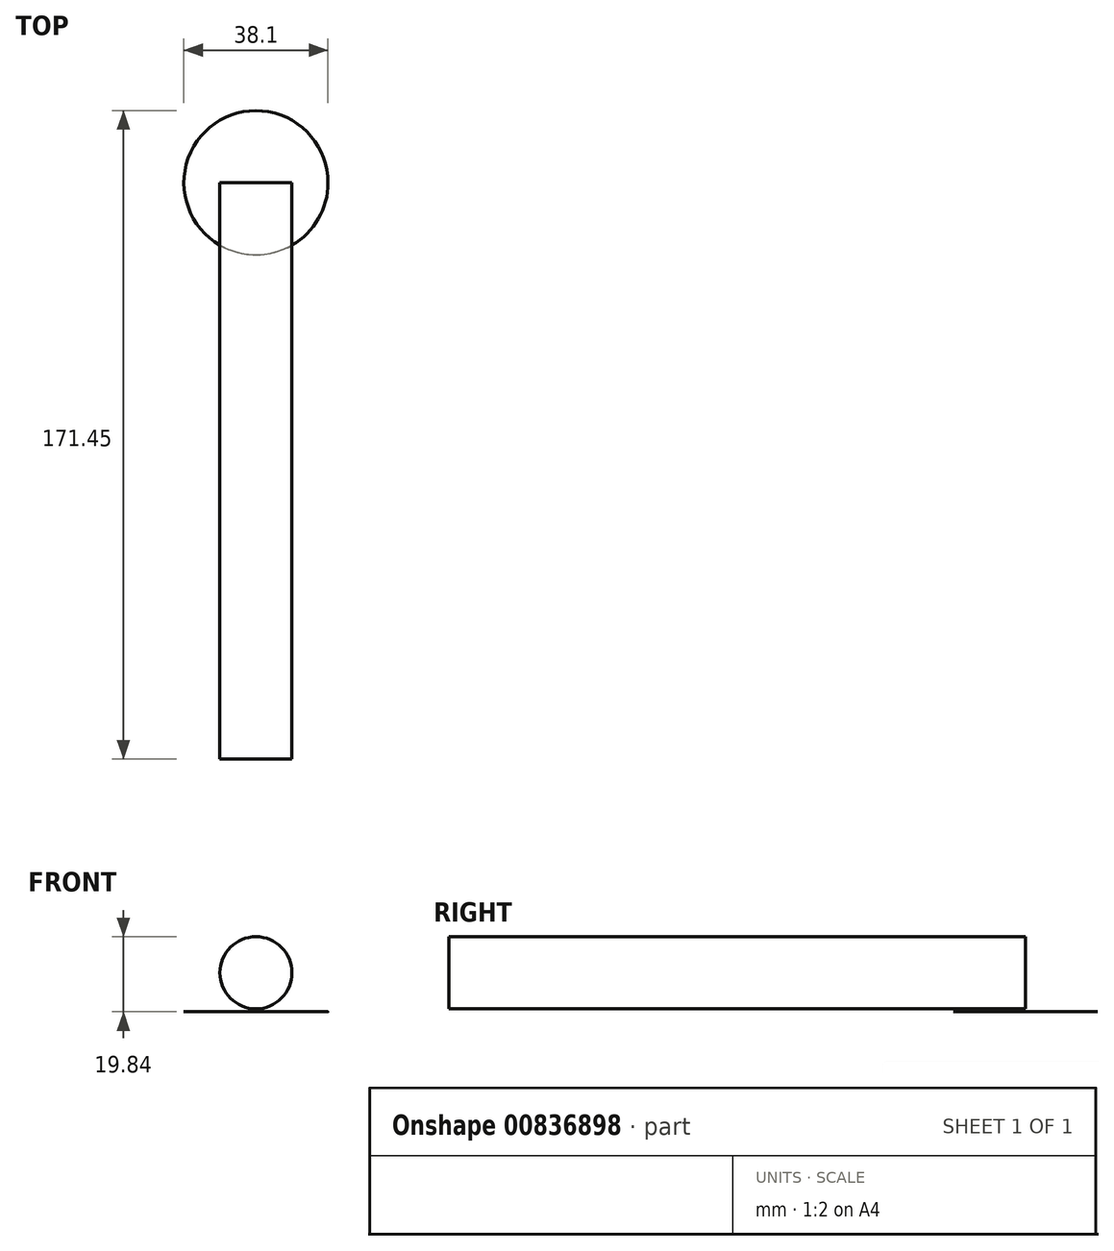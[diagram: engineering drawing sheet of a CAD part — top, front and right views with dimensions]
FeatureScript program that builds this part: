
annotation { "Feature Type Name" : "Feature", "Feature Type Description" : "" }
export const myFeature = defineFeature(function(context is Context, id is Id, definition is map)
    precondition{}
    {
        {
            var Q0;
            Q0=qCreatedBy(makeId("Top.planeOp"),FACE);
            var sketch = newSketch(context, id + "F0", { "sketchPlane" : qUnion([Q0])});
            skCircle(sketch, "E0", {"center": v(0, 0) * mm, "radius": 19.05 * mm});
            skSolve(sketch);
        }
        {
            var Q0;
            Q0=makeQuery(id+"F0.imprint","IMPRINT",FACE,{"disambiguationData":[TD([[makeQuery(id+"F0.imprint","IMPRINT",EDGE,{"derivedFrom":sQuery(id+"F0.wireOp",EDGE,"E0")}),1.0]])]});
            extrude(context, id + "F1", {"entities" : qUnion([Q0]), "depth" : 13 / 406.4 * mm, "offsetDistance" : 25.4 * mm});
        }
        {
            var Q0;
            Q0=qCreatedBy(makeId("Front.planeOp"),FACE);
            var sketch = newSketch(context, id + "F2", { "sketchPlane" : qUnion([Q0])});
            skCircle(sketch, "E1", {"center": v(0, 10.32) * mm, "radius": 9.53 * mm});
            skSolve(sketch);
        }
        {
            var Q0;
            Q0 = qSketchRegion(id + "F2", true);
            extrude(context, id + "F3", {"entities" : qUnion([Q0]), "operationType" : NewBodyOperationType.ADD, "depth" : 152.4 * mm, "offsetDistance" : 25.4 * mm});
        }
    });
